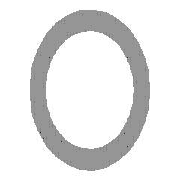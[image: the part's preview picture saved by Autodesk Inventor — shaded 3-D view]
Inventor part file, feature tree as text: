
AUTODESK INVENTOR PART (.ipt)
format: ipt  version: 2021 (Build 250183000, 183)  size: 773,120 bytes
history: native  units: mm (DEFAULTED — no unit token found)
features: other x19, plane x5, sketch x3, sweep x1, split x1
ambient origin geometry x8: Origin, YZ Plane, XZ Plane, XY Plane, X Axis, Y Axis, Z Axis, Center Point
bodies: Solid1 (feature_tree)
feature tree (29):
  parser-record x3  (decoder bookkeeping rows leaked as tree rows — omitted from the tree; the rows remain in map.json)
  other  "Driven Length"
  other  "Plano inicial"
  other  "Plano final"
  other  "Trayectoria de barrido"
  plane  "Plano de trabajo de orientación"
  sweep  "Cuerpo"
  plane  "Plano de trabajo5"
  split  "Dividir1"
  plane  "Plano de trabajo6"
  plane  "Plano de trabajo7"
  sketch  "Sketch3"  dims[d0=26.67mm d1=2.8702mm]
  plane  "Work Plane3"
  sketch  "Sketch4"  dims[d4=-0.0mm]
  sketch  "Boceto5"  dims[d5=1118.571117mm d6=90.0deg d7=1118.571117mm d8=0.0mm d9=0.0mm d18=0.0mm d19=90.0deg d20=0.0mm d21=90.0deg d74=5.0mm d75=0.0mm d76=5.0mm d77=0.0mm]
  other  "Sup7"
  other  "Sup48"
  other  "Sup49"
  other  "Sólido17"
  other  "SuperficieSolevación1"
  other  "Sup47"
  other  "Superficie de contorno31"
  other  "Superficie de contorno32"
  other  "Estructura 1617045494032.iam"
  other  "ANSI  1617061763005:1"
  other  "Marco_Bicicleta.iam"
  other  "Esqueleto_estructura:1"
note: 2 file-system paths scrubbed to <path> (originals preserved in map.json)
